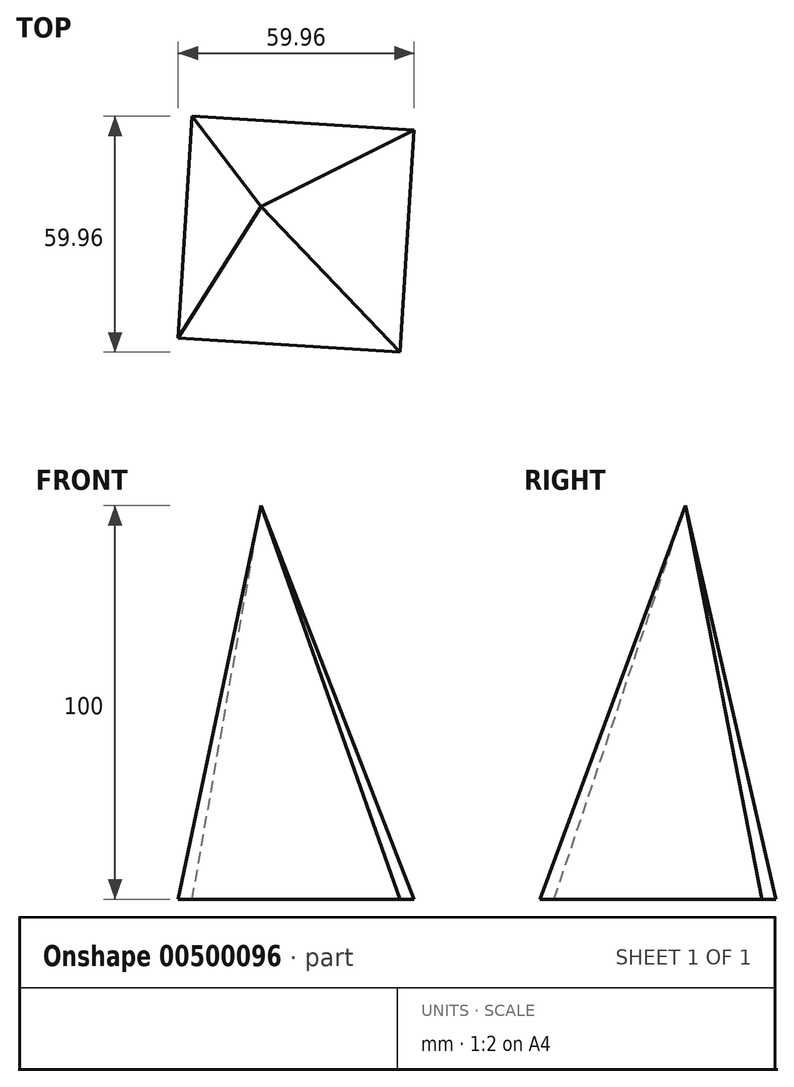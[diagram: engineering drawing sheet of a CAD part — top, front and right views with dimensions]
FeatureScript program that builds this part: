
annotation { "Feature Type Name" : "Feature", "Feature Type Description" : "" }
export const myFeature = defineFeature(function(context is Context, id is Id, definition is map)
    precondition{}
    {
        {
            var Q0;
            Q0=qCreatedBy(makeId("Top.planeOp"),FACE);
            var sketch = newSketch(context, id + "F0", { "sketchPlane" : qUnion([Q0])});
            skCircle(sketch, "E0.cCircle", {"center": v(0, 0) * mm, "radius": 39.94 * mm, "construction": true});
            skLineSegment(sketch, "E0.0", {"start": v(-26.4, 29.98) * mm, "end": v(29.98, 26.4) * mm});
            skLineSegment(sketch, "E0.1", {"start": v(29.98, 26.4) * mm, "end": v(26.4, -29.98) * mm});
            skLineSegment(sketch, "E0.2", {"start": v(26.4, -29.98) * mm, "end": v(-29.98, -26.4) * mm});
            skLineSegment(sketch, "E0.3", {"start": v(-29.98, -26.4) * mm, "end": v(-26.4, 29.98) * mm});
            skSolve(sketch);
        }
        {
            var Q0;
            Q0=qCreatedBy(makeId("Top.planeOp"),FACE);
            cPlane(context, id + "F1", {"entities" : qUnion([Q0]), "cplaneType" : CPlaneType.OFFSET, "offset" : 100 * mm, "width" : 150 * mm, "height" : 150 * mm});
        }
        {
            var Q0;
            Q0=qCreatedBy(id+"F1.planeOp",FACE);
            var sketch = newSketch(context, id + "F2", { "sketchPlane" : qUnion([Q0])});
            skPoint(sketch, "E1", {"position": v(-8.88, 6.96) * mm});
            skSolve(sketch);
        }
        {
            var Q0;
            Q0=makeQuery(id+"F0.imprint","IMPRINT",FACE,{"disambiguationData":[TD([[makeQuery(id+"F0.imprint","IMPRINT",EDGE,{"derivedFrom":sQuery(id+"F0.wireOp",EDGE,"E0.0")}),-1.0]])]});
            var Q1;
            Q1=sQuery(id+"F2.wireOp",VERTEX,"E1");
            loft(context, id + "F3", {"sheetProfilesArray" : [{ "sheetProfileEntities" : qUnion([Q0]) }, { "sheetProfileEntities" : qUnion([Q1]) }]});
        }
    });
